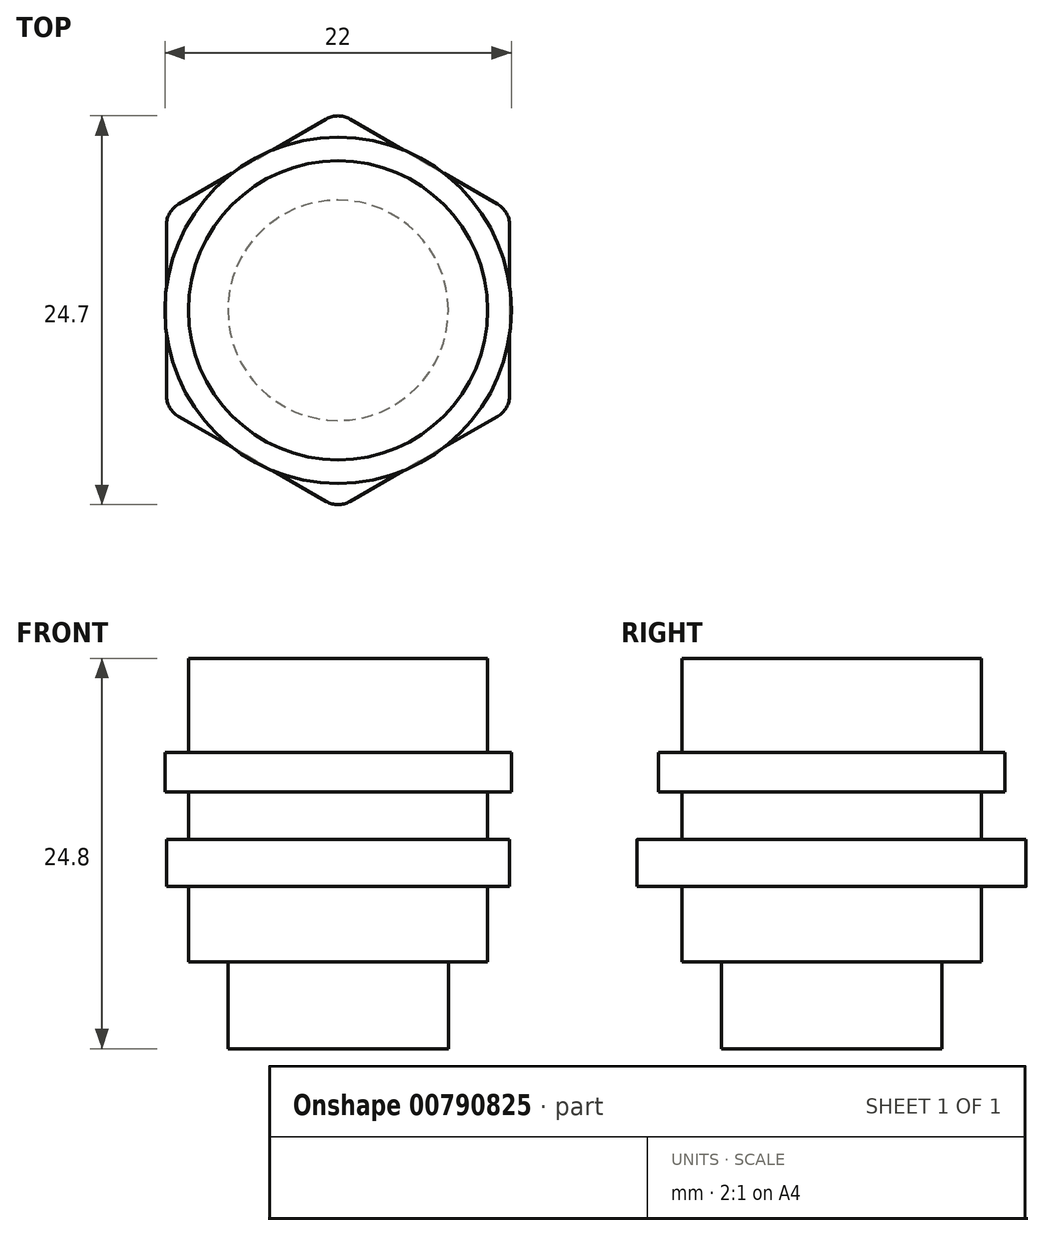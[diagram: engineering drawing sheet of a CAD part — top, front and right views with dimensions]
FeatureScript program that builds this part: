
annotation { "Feature Type Name" : "Feature", "Feature Type Description" : "" }
export const myFeature = defineFeature(function(context is Context, id is Id, definition is map)
    precondition{}
    {
        {
            var Q0;
            Q0=qCreatedBy(makeId("Top.planeOp"),FACE);
            var sketch = newSketch(context, id + "F0", { "sketchPlane" : qUnion([Q0])});
            skCircle(sketch, "E0", {"center": v(0, 0) * mm, "radius": 9.5 * mm});
            skSolve(sketch);
        }
        {
            var Q0;
            Q0 = qSketchRegion(id + "F0", true);
            extrude(context, id + "F1", {"entities" : qUnion([Q0]), "depth" : 8.5 * mm, "offsetDistance" : 25 * mm, "hasSecondDirection" : true, "secondDirectionOppositeDirection" : true, "secondDirectionDepth" : 10.8 * mm});
        }
        {
            var Q0;
            Q0=qCreatedBy(makeId("Top.planeOp"),FACE);
            var sketch = newSketch(context, id + "F2", { "sketchPlane" : qUnion([Q0])});
            skCircle(sketch, "E1", {"center": v(0, 0) * mm, "radius": 11 * mm});
            skSolve(sketch);
        }
        {
            var Q0;
            Q0 = qSketchRegion(id + "F2", true);
            extrude(context, id + "F3", {"entities" : qUnion([Q0]), "operationType" : NewBodyOperationType.ADD, "depth" : 2.5 * mm, "offsetDistance" : 25 * mm});
        }
        {
            var Q0;
            Q0=qCreatedBy(makeId("Top.planeOp"),FACE);
            cPlane(context, id + "F4", {"entities" : qUnion([Q0]), "cplaneType" : CPlaneType.OFFSET, "offset" : 3 * mm, "oppositeDirection" : true, "width" : 150 * mm, "height" : 150 * mm});
        }
        {
            var Q0;
            Q0=qCreatedBy(id+"F4.planeOp",FACE);
            var sketch = newSketch(context, id + "F5", { "sketchPlane" : qUnion([Q0])});
            skCircle(sketch, "E2.0", {"center": v(0, 0) * mm, "radius": 9.5 * mm, "construction": true});
            skCircle(sketch, "E3.cCircle", {"center": v(0, 0) * mm, "radius": 10.9 * mm, "construction": true});
            skLineSegment(sketch, "E3.0", {"start": v(0.76, 12.15) * mm, "end": v(10.14, 6.73) * mm});
            skLineSegment(sketch, "E3.1", {"start": v(10.9, 5.41) * mm, "end": v(10.9, -5.41) * mm});
            skLineSegment(sketch, "E3.2", {"start": v(10.14, -6.73) * mm, "end": v(0.76, -12.15) * mm});
            skLineSegment(sketch, "E3.3", {"start": v(-0.76, -12.15) * mm, "end": v(-10.14, -6.73) * mm});
            skLineSegment(sketch, "E3.4", {"start": v(-10.9, -5.41) * mm, "end": v(-10.9, 5.41) * mm});
            skLineSegment(sketch, "E3.5", {"start": v(-10.14, 6.73) * mm, "end": v(-0.76, 12.15) * mm});
            skPoint(sketch, "E3.0.midPoint", {"position": v(5.45, 9.44) * mm});
            skLineSegment(sketch, "E4", {"start": v(0, 0) * mm, "end": v(0, 12.59) * mm, "construction": true});
            skPoint(sketch, "E5.visualSharp", {"position": v(0, -12.59) * mm});
            skArc(sketch, "E5.filletArc", {"start": v(-0.76, -12.15) * mm, "mid": v(0, -12.35) * mm, "end": v(0.76, -12.15) * mm});
            skPoint(sketch, "E6.visualSharp", {"position": v(10.9, -6.3) * mm});
            skArc(sketch, "E6.filletArc", {"start": v(10.14, -6.73) * mm, "mid": v(10.7, -6.17) * mm, "end": v(10.9, -5.41) * mm});
            skPoint(sketch, "E7.visualSharp", {"position": v(10.9, 6.3) * mm});
            skArc(sketch, "E7.filletArc", {"start": v(10.9, 5.41) * mm, "mid": v(10.7, 6.18) * mm, "end": v(10.14, 6.73) * mm});
            skPoint(sketch, "E8.visualSharp", {"position": v(0, 12.59) * mm});
            skArc(sketch, "E8.filletArc", {"start": v(0.76, 12.15) * mm, "mid": v(0, 12.35) * mm, "end": v(-0.76, 12.15) * mm});
            skPoint(sketch, "E9.visualSharp", {"position": v(-10.9, 6.3) * mm});
            skArc(sketch, "E9.filletArc", {"start": v(-10.14, 6.73) * mm, "mid": v(-10.7, 6.18) * mm, "end": v(-10.9, 5.41) * mm});
            skPoint(sketch, "E10.visualSharp", {"position": v(-10.9, -6.3) * mm});
            skArc(sketch, "E10.filletArc", {"start": v(-10.9, -5.41) * mm, "mid": v(-10.7, -6.18) * mm, "end": v(-10.14, -6.73) * mm});
            skSolve(sketch);
        }
        {
            var Q0;
            Q0 = qSketchRegion(id + "F5", true);
            extrude(context, id + "F6", {"entities" : qUnion([Q0]), "operationType" : NewBodyOperationType.ADD, "oppositeDirection" : true, "depth" : 3 * mm, "offsetDistance" : 25 * mm});
        }
        {
            var Q0;
            Q0=makeQuery(id+"F1.opExtrude","CAP_FACE",FACE,{"disambiguationData":[OSD([sQuery(id+"F0.wireOp",EDGE,"E0")])],"isStart":true});
            var sketch = newSketch(context, id + "F7", { "sketchPlane" : qUnion([Q0])});
            skCircle(sketch, "E11", {"center": v(0, 0) * mm, "radius": 7 * mm});
            skSolve(sketch);
        }
        {
            var Q0;
            Q0 = qSketchRegion(id + "F7", true);
            extrude(context, id + "F8", {"entities" : qUnion([Q0]), "operationType" : NewBodyOperationType.ADD, "depth" : (24.8 - 10.8 - 8.5) * mm, "offsetDistance" : 25 * mm});
        }
    });
